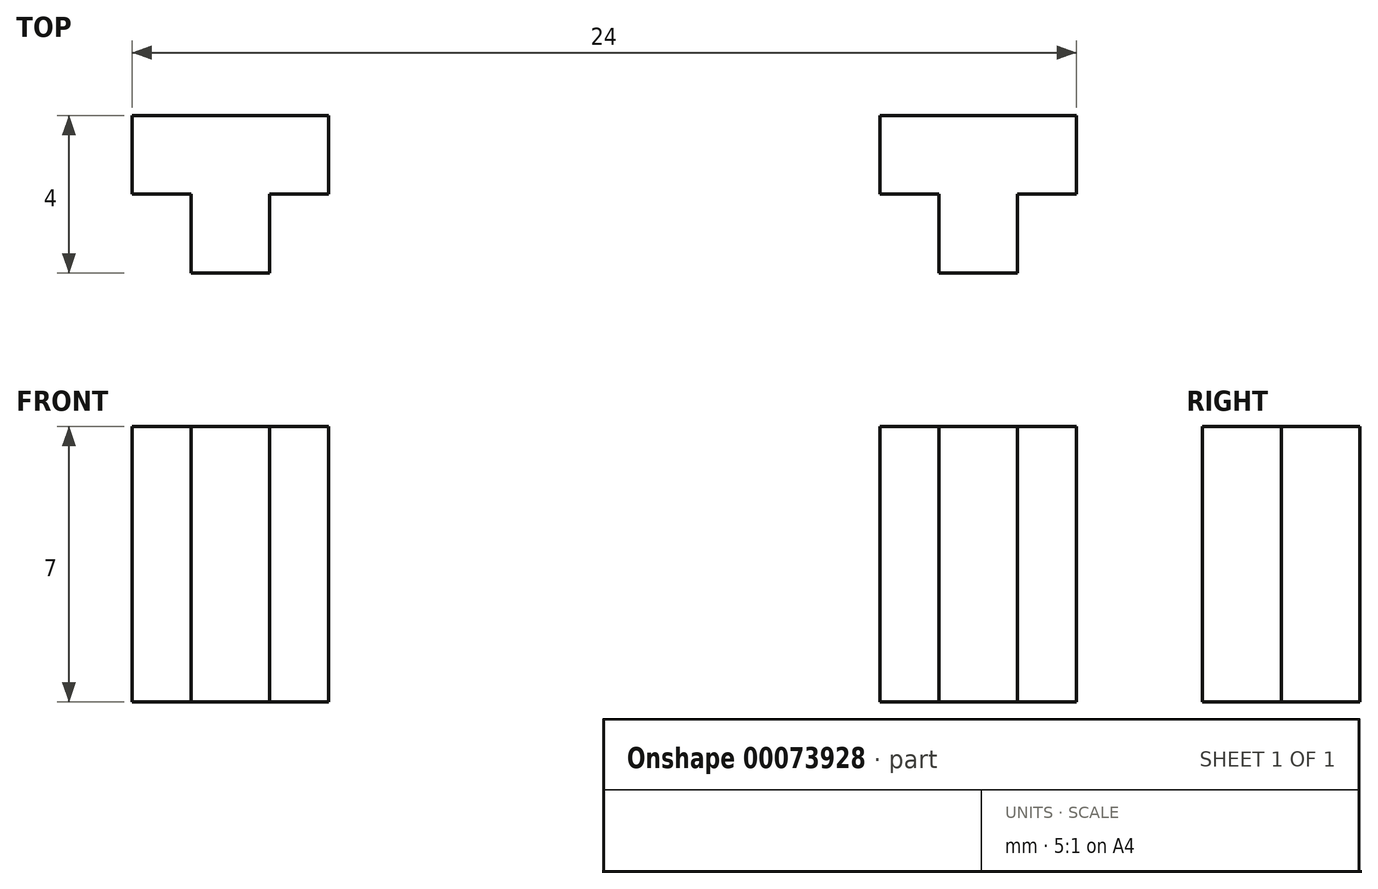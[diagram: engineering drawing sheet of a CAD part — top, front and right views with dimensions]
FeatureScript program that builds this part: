
annotation { "Feature Type Name" : "Feature", "Feature Type Description" : "" }
export const myFeature = defineFeature(function(context is Context, id is Id, definition is map)
    precondition{}
    {
        {
            assignVariable(context, id + "F0", {"name" : "height", "anyValue" : 7});
        }
        {
            var Q0;
            Q0=qCreatedBy(makeId("Top.planeOp"),FACE);
            var sketch = newSketch(context, id + "F1", { "sketchPlane" : qUnion([Q0])});
            skLineSegment(sketch, "E0", {"start": v(10.5, 0) * mm, "end": v(10.5, 2) * mm});
            skLineSegment(sketch, "E1", {"start": v(10.5, 2) * mm, "end": v(12, 2) * mm});
            skLineSegment(sketch, "E2", {"start": v(12, 2) * mm, "end": v(12, 4) * mm});
            skLineSegment(sketch, "E3", {"start": v(10.5, 0) * mm, "end": v(9.5, 0) * mm});
            skLineSegment(sketch, "E4", {"start": v(9.5, 0) * mm, "end": v(9.5, 4) * mm});
            skLineSegment(sketch, "E5", {"start": v(12, 4) * mm, "end": v(9.5, 4) * mm});
            skSolve(sketch);
        }
        {
            var Q0;
            Q0=makeQuery(id+"F1.imprint","IMPRINT",FACE,{"disambiguationData":[TD([[makeQuery(id+"F1.imprint","IMPRINT",EDGE,{"derivedFrom":sQuery(id+"F1.wireOp",EDGE,"E0")}),1.0]])]});
            extrude(context, id + "F2", {"entities" : qUnion([Q0]), "depth" : (getVariable(context, 'height')) * mm});
        }
        {
            var Q0;
            Q0=makeQuery(id+"F2.opExtrude","SWEPT_BODY",BODY,{"disambiguationData":[OSD([sQuery(id+"F1.wireOp",EDGE,"E0"),sQuery(id+"F1.wireOp",EDGE,"E1"),sQuery(id+"F1.wireOp",EDGE,"E2"),sQuery(id+"F1.wireOp",EDGE,"E3"),sQuery(id+"F1.wireOp",EDGE,"E4"),sQuery(id+"F1.wireOp",EDGE,"E5")])]});
            var Q1;
            Q1=makeQuery(id+"F2.opExtrude","SWEPT_FACE",FACE,{"disambiguationData":[OSD([sQuery(id+"F1.wireOp",EDGE,"E4")])]});
            mirror(context, id + "F3", {"operationType" : NewBodyOperationType.ADD, "entities" : qUnion([Q0]), "mirrorPlane" : qUnion([Q1])});
        }
        {
            var Q0;
            Q0=makeQuery(id+"F2.opExtrude","SWEPT_BODY",BODY,{"disambiguationData":[OSD([sQuery(id+"F1.wireOp",EDGE,"E0"),sQuery(id+"F1.wireOp",EDGE,"E1"),sQuery(id+"F1.wireOp",EDGE,"E2"),sQuery(id+"F1.wireOp",EDGE,"E3"),sQuery(id+"F1.wireOp",EDGE,"E4"),sQuery(id+"F1.wireOp",EDGE,"E5")])]});
            var Q1;
            Q1=qCreatedBy(makeId("Right.planeOp"),FACE);
            mirror(context, id + "F4", {"operationType" : NewBodyOperationType.ADD, "entities" : qUnion([Q0]), "mirrorPlane" : qUnion([Q1])});
        }
    });
